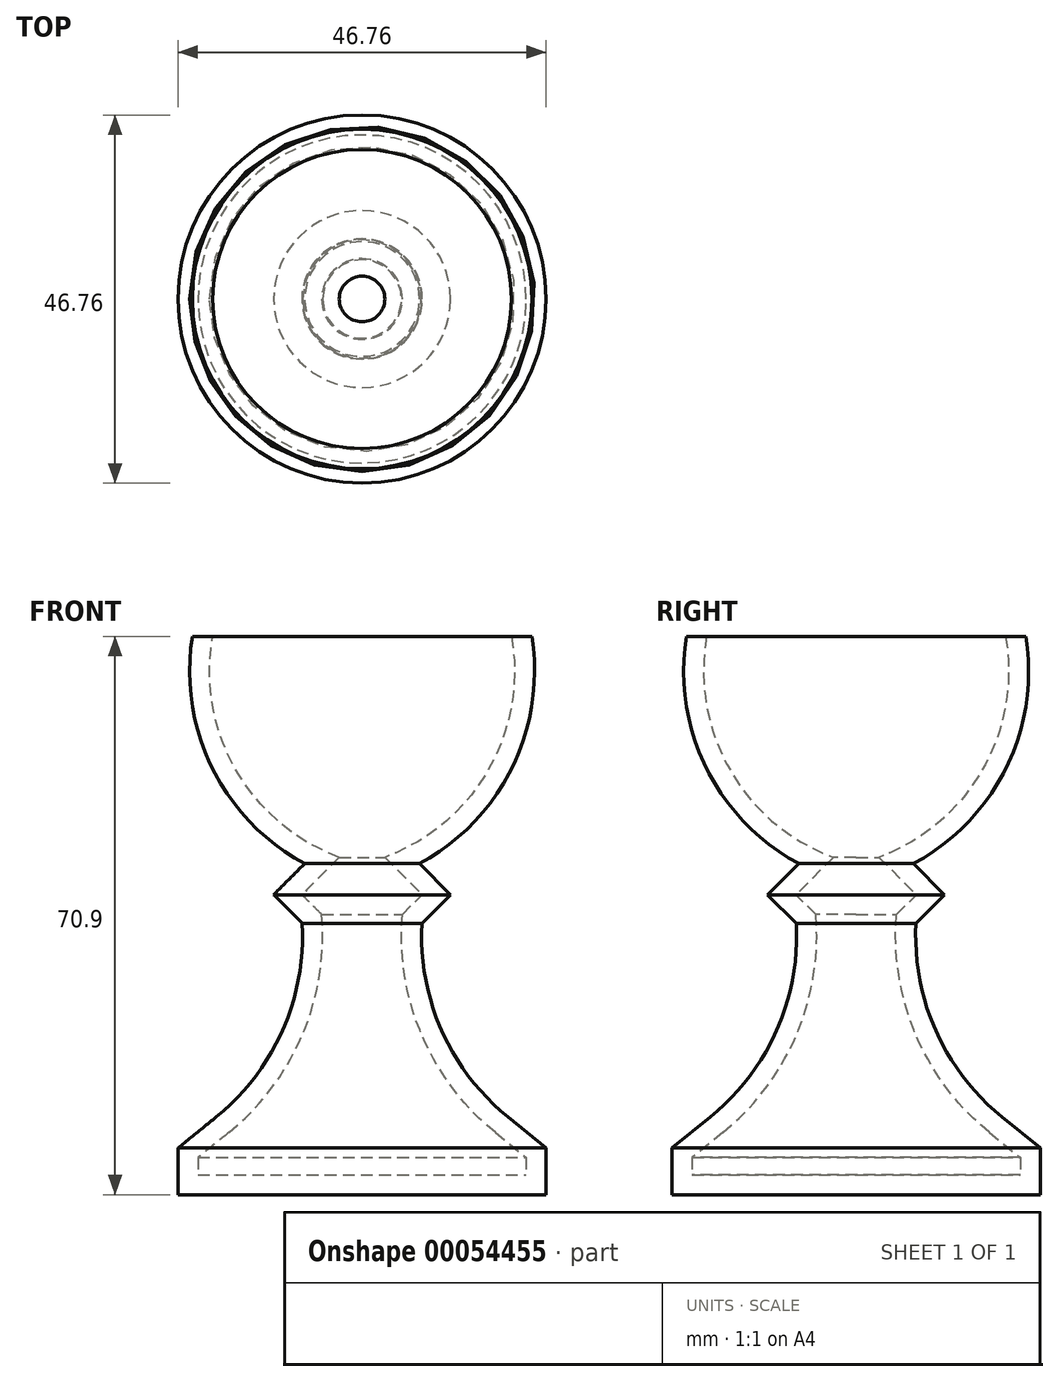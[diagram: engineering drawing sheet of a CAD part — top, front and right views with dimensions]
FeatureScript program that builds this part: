
annotation { "Feature Type Name" : "Feature", "Feature Type Description" : "" }
export const myFeature = defineFeature(function(context is Context, id is Id, definition is map)
    precondition{}
    {
        {
            var Q0;
            Q0=qCreatedBy(makeId("Front.planeOp"),FACE);
            var sketch = newSketch(context, id + "F0", { "sketchPlane" : qUnion([Q0])});
            skLineSegment(sketch, "E0", {"start": v(0, 0) * mm, "end": v(23.38, 0) * mm});
            skLineSegment(sketch, "E1", {"start": v(23.38, 0) * mm, "end": v(23.38, 5.92) * mm});
            skLineSegment(sketch, "E2", {"start": v(23.38, 5.92) * mm, "end": v(18.52, 9.87) * mm});
            skArc(sketch, "E3", {"start": v(7.6, 34.46) * mm, "mid": v(10.11, 20.86) * mm, "end": v(18.52, 9.87) * mm});
            skLineSegment(sketch, "E4", {"start": v(7.6, 34.46) * mm, "end": v(11.23, 38.1) * mm});
            skLineSegment(sketch, "E5", {"start": v(11.23, 38.1) * mm, "end": v(7.29, 42.05) * mm});
            skLineSegment(sketch, "E6", {"start": v(0, 0) * mm, "end": v(0, 70.9) * mm});
            skLineSegment(sketch, "E7", {"start": v(0, 70.9) * mm, "end": v(21.56, 70.9) * mm});
            skArc(sketch, "E8", {"start": v(7.29, 42.05) * mm, "mid": v(19.03, 54.2) * mm, "end": v(21.56, 70.9) * mm});
            skSolve(sketch);
        }
        {
            var Q0;
            Q0=makeQuery(id+"F0.imprint","IMPRINT",FACE,{"disambiguationData":[TD([[makeQuery(id+"F0.imprint","IMPRINT",EDGE,{"derivedFrom":sQuery(id+"F0.wireOp",EDGE,"E0")}),1.0]])]});
            var Q1;
            Q1=sQuery(id+"F0.wireOp",EDGE,"E6");
            revolve(context, id + "F1", {"entities" : qUnion([Q0]), "axis" : qUnion([Q1]), "revolveType" : RevolveType.FULL});
        }
        {
            var Q0;
            Q0=makeQuery(id+"F1.opRevolve","SWEPT_FACE",FACE,{"disambiguationData":[OSD([sQuery(id+"F0.wireOp",EDGE,"E7")])]});
            shell(context, id + "F2", {"entities" : qUnion([Q0]), "thickness" : 2.54 * mm});
        }
    });
